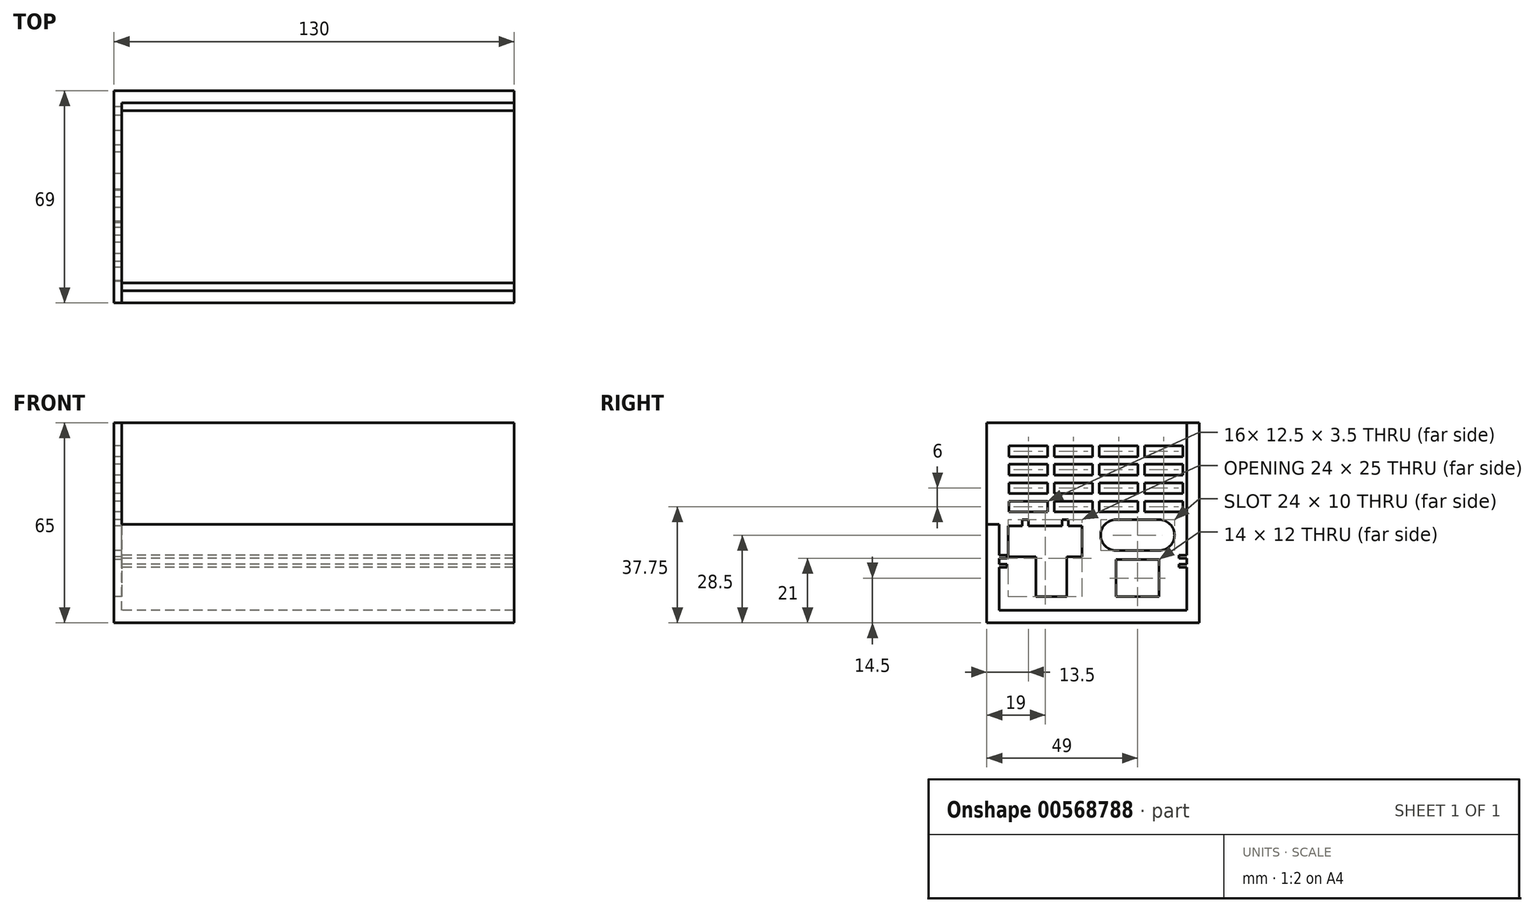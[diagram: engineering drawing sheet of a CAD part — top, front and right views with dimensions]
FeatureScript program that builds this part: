
annotation { "Feature Type Name" : "Feature", "Feature Type Description" : "" }
export const myFeature = defineFeature(function(context is Context, id is Id, definition is map)
    precondition{}
    {
        {
            var Q0;
            Q0=qCreatedBy(makeId("Right.planeOp"),FACE);
            var sketch = newSketch(context, id + "F0", { "sketchPlane" : qUnion([Q0])});
            skLineSegment(sketch, "E0", {"start": v(0, 0) * mm, "end": v(69, 0) * mm});
            skLineSegment(sketch, "E1", {"start": v(4, 4) * mm, "end": v(4, 18) * mm});
            skLineSegment(sketch, "E2", {"start": v(4, 18) * mm, "end": v(6.5, 18) * mm});
            skLineSegment(sketch, "E3", {"start": v(6.5, 18) * mm, "end": v(6.5, 19) * mm});
            skLineSegment(sketch, "E4", {"start": v(6.5, 19) * mm, "end": v(4, 19) * mm});
            skLineSegment(sketch, "E5", {"start": v(4, 19) * mm, "end": v(4, 21) * mm});
            skLineSegment(sketch, "E6", {"start": v(4, 21) * mm, "end": v(6.5, 21) * mm});
            skLineSegment(sketch, "E7", {"start": v(6.5, 21) * mm, "end": v(6.5, 22) * mm});
            skLineSegment(sketch, "E8", {"start": v(6.5, 22) * mm, "end": v(4, 22) * mm});
            skLineSegment(sketch, "E9", {"start": v(4, 22) * mm, "end": v(4, 32) * mm});
            skLineSegment(sketch, "E10", {"start": v(4, 32) * mm, "end": v(0, 32) * mm});
            skLineSegment(sketch, "E11", {"start": v(0, 32) * mm, "end": v(0, 0) * mm});
            skLineSegment(sketch, "E12", {"start": v(4, 4) * mm, "end": v(65, 4) * mm});
            skLineSegment(sketch, "E13", {"start": v(65, 4) * mm, "end": v(65, 18) * mm});
            skLineSegment(sketch, "E14", {"start": v(65, 4) * mm, "end": v(65, 0) * mm, "construction": true});
            skLineSegment(sketch, "E15", {"start": v(65, 18) * mm, "end": v(62.5, 18) * mm});
            skLineSegment(sketch, "E16", {"start": v(62.5, 18) * mm, "end": v(62.5, 19) * mm});
            skLineSegment(sketch, "E17", {"start": v(62.5, 19) * mm, "end": v(65, 19) * mm});
            skLineSegment(sketch, "E18", {"start": v(65, 19) * mm, "end": v(65, 21) * mm});
            skLineSegment(sketch, "E19", {"start": v(65, 21) * mm, "end": v(62.5, 21) * mm});
            skLineSegment(sketch, "E20", {"start": v(62.5, 21) * mm, "end": v(62.5, 22) * mm});
            skLineSegment(sketch, "E21", {"start": v(62.5, 22) * mm, "end": v(65, 22) * mm});
            skLineSegment(sketch, "E22", {"start": v(65, 22) * mm, "end": v(65, 65) * mm});
            skLineSegment(sketch, "E23", {"start": v(65, 65) * mm, "end": v(69, 65) * mm});
            skLineSegment(sketch, "E24", {"start": v(69, 65) * mm, "end": v(69, 0) * mm});
            skSolve(sketch);
        }
        {
            var Q0;
            Q0=makeQuery(id+"F0.imprint","IMPRINT",FACE,{"disambiguationData":[TD([[makeQuery(id+"F0.imprint","IMPRINT",EDGE,{"derivedFrom":sQuery(id+"F0.wireOp",EDGE,"E0")}),1.0]])]});
            extrude(context, id + "F1", {"entities" : qUnion([Q0]), "depth" : 130 * mm, "offsetDistance" : 25 * mm});
        }
        {
            var Q0;
            Q0=makeQuery(id+"F1.opExtrude","CAP_FACE",FACE,{"disambiguationData":[OSD([sQuery(id+"F0.wireOp",EDGE,"E0"),sQuery(id+"F0.wireOp",EDGE,"E1"),sQuery(id+"F0.wireOp",EDGE,"E2"),sQuery(id+"F0.wireOp",EDGE,"E3"),sQuery(id+"F0.wireOp",EDGE,"E4"),sQuery(id+"F0.wireOp",EDGE,"E5"),sQuery(id+"F0.wireOp",EDGE,"E6"),sQuery(id+"F0.wireOp",EDGE,"E7"),sQuery(id+"F0.wireOp",EDGE,"E8"),sQuery(id+"F0.wireOp",EDGE,"E9"),sQuery(id+"F0.wireOp",EDGE,"E10"),sQuery(id+"F0.wireOp",EDGE,"E11"),sQuery(id+"F0.wireOp",EDGE,"E12"),sQuery(id+"F0.wireOp",EDGE,"E13"),sQuery(id+"F0.wireOp",EDGE,"E15"),sQuery(id+"F0.wireOp",EDGE,"E16"),sQuery(id+"F0.wireOp",EDGE,"E17"),sQuery(id+"F0.wireOp",EDGE,"E18"),sQuery(id+"F0.wireOp",EDGE,"E19"),sQuery(id+"F0.wireOp",EDGE,"E20"),sQuery(id+"F0.wireOp",EDGE,"E21"),sQuery(id+"F0.wireOp",EDGE,"E22"),sQuery(id+"F0.wireOp",EDGE,"E23"),sQuery(id+"F0.wireOp",EDGE,"E24")])],"isStart":true});
            var sketch = newSketch(context, id + "F2", { "sketchPlane" : qUnion([Q0])});
            skLineSegment(sketch, "E25.bottom", {"start": v(0, 0) * mm, "end": v(-69, 0) * mm});
            skLineSegment(sketch, "E25.top", {"start": v(0, 65) * mm, "end": v(-69, 65) * mm});
            skLineSegment(sketch, "E25.left", {"start": v(0, 0) * mm, "end": v(0, 65) * mm});
            skLineSegment(sketch, "E25.right", {"start": v(-69, 0) * mm, "end": v(-69, 65) * mm});
            skLineSegment(sketch, "E26", {"start": v(-7, 31.5) * mm, "end": v(-7, 21.5) * mm});
            skLineSegment(sketch, "E27", {"start": v(-7, 21.5) * mm, "end": v(-16, 21.5) * mm});
            skLineSegment(sketch, "E28", {"start": v(-16, 21.5) * mm, "end": v(-16, 8.5) * mm});
            skLineSegment(sketch, "E29", {"start": v(-16, 8.5) * mm, "end": v(-26, 8.5) * mm});
            skLineSegment(sketch, "E30", {"start": v(-26, 8.5) * mm, "end": v(-26, 21.5) * mm});
            skLineSegment(sketch, "E31", {"start": v(-26, 21.5) * mm, "end": v(-31, 21.5) * mm});
            skLineSegment(sketch, "E32", {"start": v(-31, 21.5) * mm, "end": v(-31, 31.5) * mm});
            skLineSegment(sketch, "E33.bottom", {"start": v(-56, 20.5) * mm, "end": v(-42, 20.5) * mm});
            skLineSegment(sketch, "E33.top", {"start": v(-56, 8.5) * mm, "end": v(-42, 8.5) * mm});
            skLineSegment(sketch, "E33.left", {"start": v(-56, 20.5) * mm, "end": v(-56, 8.5) * mm});
            skLineSegment(sketch, "E33.right", {"start": v(-42, 20.5) * mm, "end": v(-42, 8.5) * mm});
            skLineSegment(sketch, "E34.bottom", {"start": v(-56, 23.5) * mm, "end": v(-42, 23.5) * mm});
            skLineSegment(sketch, "E34.top", {"start": v(-56, 33.5) * mm, "end": v(-42, 33.5) * mm});
            skArc(sketch, "E35", {"start": v(-42, 33.5) * mm, "mid": v(-37, 28.5) * mm, "end": v(-42, 23.5) * mm});
            skArc(sketch, "E36", {"start": v(-56, 33.5) * mm, "mid": v(-61, 28.5) * mm, "end": v(-56, 23.5) * mm});
            skLineSegment(sketch, "E37", {"start": v(-56, 20.5) * mm, "end": v(-56, 23.5) * mm, "construction": true});
            skLineSegment(sketch, "E38", {"start": v(-56, 33.5) * mm, "end": v(-56, 23.5) * mm, "construction": true});
            skLineSegment(sketch, "E39", {"start": v(-42, 33.5) * mm, "end": v(-42, 23.5) * mm, "construction": true});
            skLineSegment(sketch, "E40", {"start": v(-31, 31.5) * mm, "end": v(-26.5, 31.5) * mm});
            skLineSegment(sketch, "E41", {"start": v(-26.5, 31.5) * mm, "end": v(-26.5, 33.5) * mm});
            skLineSegment(sketch, "E42", {"start": v(-26.5, 33.5) * mm, "end": v(-24.5, 33.5) * mm});
            skLineSegment(sketch, "E43", {"start": v(-24.5, 33.5) * mm, "end": v(-24.5, 31.5) * mm});
            skLineSegment(sketch, "E44", {"start": v(-24.5, 31.5) * mm, "end": v(-13.5, 31.5) * mm});
            skLineSegment(sketch, "E45", {"start": v(-13.5, 31.5) * mm, "end": v(-13.5, 33.5) * mm});
            skLineSegment(sketch, "E46", {"start": v(-13.5, 33.5) * mm, "end": v(-11.5, 33.5) * mm});
            skLineSegment(sketch, "E47", {"start": v(-11.5, 33.5) * mm, "end": v(-11.5, 31.5) * mm});
            skLineSegment(sketch, "E48", {"start": v(-11.5, 31.5) * mm, "end": v(-7, 31.5) * mm});
            skLineSegment(sketch, "E49", {"start": v(-31, 31.5) * mm, "end": v(-7, 31.5) * mm, "construction": true});
            skLineSegment(sketch, "E50.bottom", {"start": v(-63.75, 57.5) * mm, "end": v(-51.25, 57.5) * mm});
            skLineSegment(sketch, "E50.top", {"start": v(-63.75, 54) * mm, "end": v(-51.25, 54) * mm});
            skLineSegment(sketch, "E50.left", {"start": v(-63.75, 57.5) * mm, "end": v(-63.75, 54) * mm});
            skLineSegment(sketch, "E50.right", {"start": v(-51.25, 57.5) * mm, "end": v(-51.25, 54) * mm});
            skLineSegment(sketch, "E51.1.0.0", {"start": v(-63.75, 51.5) * mm, "end": v(-51.25, 51.5) * mm});
            skLineSegment(sketch, "E51.1.0.1", {"start": v(-63.75, 51.5) * mm, "end": v(-63.75, 48) * mm});
            skLineSegment(sketch, "E51.1.0.2", {"start": v(-63.75, 48) * mm, "end": v(-51.25, 48) * mm});
            skLineSegment(sketch, "E51.1.0.3", {"start": v(-51.25, 51.5) * mm, "end": v(-51.25, 48) * mm});
            skLineSegment(sketch, "E51.2.0.0", {"start": v(-63.75, 45.5) * mm, "end": v(-51.25, 45.5) * mm});
            skLineSegment(sketch, "E51.2.0.1", {"start": v(-63.75, 45.5) * mm, "end": v(-63.75, 42) * mm});
            skLineSegment(sketch, "E51.2.0.2", {"start": v(-63.75, 42) * mm, "end": v(-51.25, 42) * mm});
            skLineSegment(sketch, "E51.2.0.3", {"start": v(-51.25, 45.5) * mm, "end": v(-51.25, 42) * mm});
            skLineSegment(sketch, "E51.3.0.0", {"start": v(-63.75, 39.5) * mm, "end": v(-51.25, 39.5) * mm});
            skLineSegment(sketch, "E51.3.0.1", {"start": v(-63.75, 39.5) * mm, "end": v(-63.75, 36) * mm});
            skLineSegment(sketch, "E51.3.0.2", {"start": v(-63.75, 36) * mm, "end": v(-51.25, 36) * mm});
            skLineSegment(sketch, "E51.3.0.3", {"start": v(-51.25, 39.5) * mm, "end": v(-51.25, 36) * mm});
            skLineSegment(sketch, "E51.direction1", {"start": v(-63.75, 54) * mm, "end": v(-63.75, 48) * mm, "construction": true});
            skLineSegment(sketch, "E52", {"start": v(-56, 33.5) * mm, "end": v(-56, 36) * mm, "construction": true});
            skLineSegment(sketch, "E53", {"start": v(-63.75, 42) * mm, "end": v(-63.75, 39.5) * mm, "construction": true});
            skLineSegment(sketch, "E54.1.0.0", {"start": v(-49.08, 57.5) * mm, "end": v(-36.58, 57.5) * mm});
            skLineSegment(sketch, "E54.1.0.1", {"start": v(-49.08, 57.5) * mm, "end": v(-49.08, 54) * mm});
            skLineSegment(sketch, "E54.1.0.2", {"start": v(-49.08, 54) * mm, "end": v(-36.58, 54) * mm});
            skLineSegment(sketch, "E54.1.0.3", {"start": v(-36.58, 57.5) * mm, "end": v(-36.58, 54) * mm});
            skLineSegment(sketch, "E54.2.0.0", {"start": v(-34.42, 57.5) * mm, "end": v(-21.92, 57.5) * mm});
            skLineSegment(sketch, "E54.2.0.1", {"start": v(-34.42, 57.5) * mm, "end": v(-34.42, 54) * mm});
            skLineSegment(sketch, "E54.2.0.2", {"start": v(-34.42, 54) * mm, "end": v(-21.92, 54) * mm});
            skLineSegment(sketch, "E54.2.0.3", {"start": v(-21.92, 57.5) * mm, "end": v(-21.92, 54) * mm});
            skLineSegment(sketch, "E54.3.0.0", {"start": v(-19.75, 57.5) * mm, "end": v(-7.25, 57.5) * mm});
            skLineSegment(sketch, "E54.3.0.1", {"start": v(-19.75, 57.5) * mm, "end": v(-19.75, 54) * mm});
            skLineSegment(sketch, "E54.3.0.2", {"start": v(-19.75, 54) * mm, "end": v(-7.25, 54) * mm});
            skLineSegment(sketch, "E54.3.0.3", {"start": v(-7.25, 57.5) * mm, "end": v(-7.25, 54) * mm});
            skLineSegment(sketch, "E54.direction1", {"start": v(-63.75, 54) * mm, "end": v(-49.08, 54) * mm, "construction": true});
            skLineSegment(sketch, "E55.1.0.0", {"start": v(-49.08, 48) * mm, "end": v(-36.58, 48) * mm});
            skLineSegment(sketch, "E55.1.0.1", {"start": v(-36.58, 51.5) * mm, "end": v(-36.58, 48) * mm});
            skLineSegment(sketch, "E55.1.0.2", {"start": v(-49.08, 51.5) * mm, "end": v(-36.58, 51.5) * mm});
            skLineSegment(sketch, "E55.1.0.3", {"start": v(-49.08, 51.5) * mm, "end": v(-49.08, 48) * mm});
            skLineSegment(sketch, "E55.2.0.0", {"start": v(-34.42, 48) * mm, "end": v(-21.92, 48) * mm});
            skLineSegment(sketch, "E55.2.0.1", {"start": v(-21.92, 51.5) * mm, "end": v(-21.92, 48) * mm});
            skLineSegment(sketch, "E55.2.0.2", {"start": v(-34.42, 51.5) * mm, "end": v(-21.92, 51.5) * mm});
            skLineSegment(sketch, "E55.2.0.3", {"start": v(-34.42, 51.5) * mm, "end": v(-34.42, 48) * mm});
            skLineSegment(sketch, "E55.3.0.0", {"start": v(-19.75, 48) * mm, "end": v(-7.25, 48) * mm});
            skLineSegment(sketch, "E55.3.0.1", {"start": v(-7.25, 51.5) * mm, "end": v(-7.25, 48) * mm});
            skLineSegment(sketch, "E55.3.0.2", {"start": v(-19.75, 51.5) * mm, "end": v(-7.25, 51.5) * mm});
            skLineSegment(sketch, "E55.3.0.3", {"start": v(-19.75, 51.5) * mm, "end": v(-19.75, 48) * mm});
            skLineSegment(sketch, "E55.direction1", {"start": v(-63.75, 48) * mm, "end": v(-49.08, 48) * mm, "construction": true});
            skLineSegment(sketch, "E56.1.0.0", {"start": v(-49.08, 45.5) * mm, "end": v(-49.08, 42) * mm});
            skLineSegment(sketch, "E56.1.0.1", {"start": v(-49.08, 42) * mm, "end": v(-36.58, 42) * mm});
            skLineSegment(sketch, "E56.1.0.2", {"start": v(-36.58, 45.5) * mm, "end": v(-36.58, 42) * mm});
            skLineSegment(sketch, "E56.1.0.3", {"start": v(-49.08, 45.5) * mm, "end": v(-36.58, 45.5) * mm});
            skLineSegment(sketch, "E56.2.0.0", {"start": v(-34.42, 45.5) * mm, "end": v(-34.42, 42) * mm});
            skLineSegment(sketch, "E56.2.0.1", {"start": v(-34.42, 42) * mm, "end": v(-21.92, 42) * mm});
            skLineSegment(sketch, "E56.2.0.2", {"start": v(-21.92, 45.5) * mm, "end": v(-21.92, 42) * mm});
            skLineSegment(sketch, "E56.2.0.3", {"start": v(-34.42, 45.5) * mm, "end": v(-21.92, 45.5) * mm});
            skLineSegment(sketch, "E56.3.0.0", {"start": v(-19.75, 45.5) * mm, "end": v(-19.75, 42) * mm});
            skLineSegment(sketch, "E56.3.0.1", {"start": v(-19.75, 42) * mm, "end": v(-7.25, 42) * mm});
            skLineSegment(sketch, "E56.3.0.2", {"start": v(-7.25, 45.5) * mm, "end": v(-7.25, 42) * mm});
            skLineSegment(sketch, "E56.3.0.3", {"start": v(-19.75, 45.5) * mm, "end": v(-7.25, 45.5) * mm});
            skLineSegment(sketch, "E56.direction1", {"start": v(-63.75, 42) * mm, "end": v(-49.08, 42) * mm, "construction": true});
            skLineSegment(sketch, "E57.1.0.0", {"start": v(-49.08, 36) * mm, "end": v(-36.58, 36) * mm});
            skLineSegment(sketch, "E57.1.0.1", {"start": v(-49.08, 39.5) * mm, "end": v(-49.08, 36) * mm});
            skLineSegment(sketch, "E57.1.0.2", {"start": v(-36.58, 39.5) * mm, "end": v(-36.58, 36) * mm});
            skLineSegment(sketch, "E57.1.0.3", {"start": v(-49.08, 39.5) * mm, "end": v(-36.58, 39.5) * mm});
            skLineSegment(sketch, "E57.2.0.0", {"start": v(-34.42, 36) * mm, "end": v(-21.92, 36) * mm});
            skLineSegment(sketch, "E57.2.0.1", {"start": v(-34.42, 39.5) * mm, "end": v(-34.42, 36) * mm});
            skLineSegment(sketch, "E57.2.0.2", {"start": v(-21.92, 39.5) * mm, "end": v(-21.92, 36) * mm});
            skLineSegment(sketch, "E57.2.0.3", {"start": v(-34.42, 39.5) * mm, "end": v(-21.92, 39.5) * mm});
            skLineSegment(sketch, "E57.3.0.0", {"start": v(-19.75, 36) * mm, "end": v(-7.25, 36) * mm});
            skLineSegment(sketch, "E57.3.0.1", {"start": v(-19.75, 39.5) * mm, "end": v(-19.75, 36) * mm});
            skLineSegment(sketch, "E57.3.0.2", {"start": v(-7.25, 39.5) * mm, "end": v(-7.25, 36) * mm});
            skLineSegment(sketch, "E57.3.0.3", {"start": v(-19.75, 39.5) * mm, "end": v(-7.25, 39.5) * mm});
            skLineSegment(sketch, "E57.direction1", {"start": v(-63.75, 36) * mm, "end": v(-49.08, 36) * mm, "construction": true});
            skSolve(sketch);
        }
        {
            var Q0;
            Q0=makeQuery(id+"F2.imprint","IMPRINT",FACE,{"disambiguationData":[TD([[makeQuery(id+"F2.imprint","IMPRINT",EDGE,{"derivedFrom":sQuery(id+"F2.wireOp",EDGE,"E26")}),1.0]])]});
            extrude(context, id + "F3", {"entities" : qUnion([Q0]), "operationType" : NewBodyOperationType.ADD, "oppositeDirection" : true, "depth" : 2.5 * mm, "offsetDistance" : 25 * mm});
        }
    });
